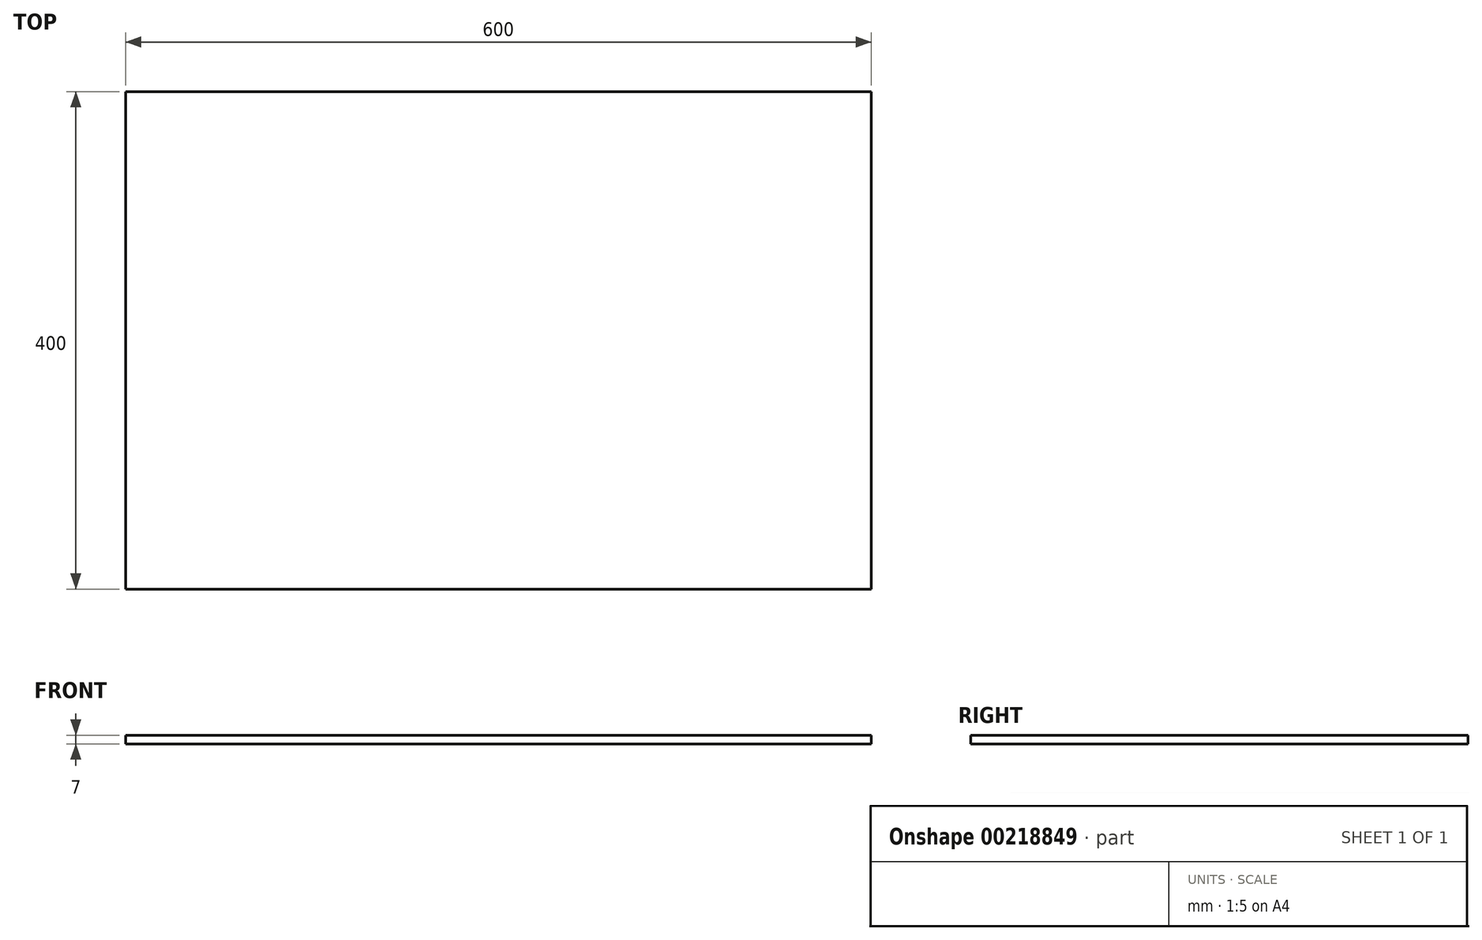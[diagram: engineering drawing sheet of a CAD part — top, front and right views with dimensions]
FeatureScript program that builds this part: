
annotation { "Feature Type Name" : "Feature", "Feature Type Description" : "" }
export const myFeature = defineFeature(function(context is Context, id is Id, definition is map)
    precondition{}
    {
        {
            var Q0;
            Q0=qCreatedBy(makeId("Top.planeOp"),FACE);
            var sketch = newSketch(context, id + "F0", { "sketchPlane" : qUnion([Q0])});
            skLineSegment(sketch, "E0.bottom", {"start": v(300, 200) * mm, "end": v(-300, 200) * mm});
            skLineSegment(sketch, "E0.top", {"start": v(300, -200) * mm, "end": v(-300, -200) * mm});
            skLineSegment(sketch, "E0.left", {"start": v(300, 200) * mm, "end": v(300, -200) * mm});
            skLineSegment(sketch, "E0.right", {"start": v(-300, 200) * mm, "end": v(-300, -200) * mm});
            skPoint(sketch, "E0.middle", {"position": v(0, 0) * mm});
            skSolve(sketch);
        }
        {
            var Q0;
            Q0=makeQuery(id+"F0.imprint","IMPRINT",FACE,{"disambiguationData":[TD([[makeQuery(id+"F0.imprint","IMPRINT",EDGE,{"derivedFrom":sQuery(id+"F0.wireOp",EDGE,"E0.bottom")}),1.0]])]});
            extrude(context, id + "F1", {"entities" : qUnion([Q0]), "depth" : 7 * mm});
        }
    });
